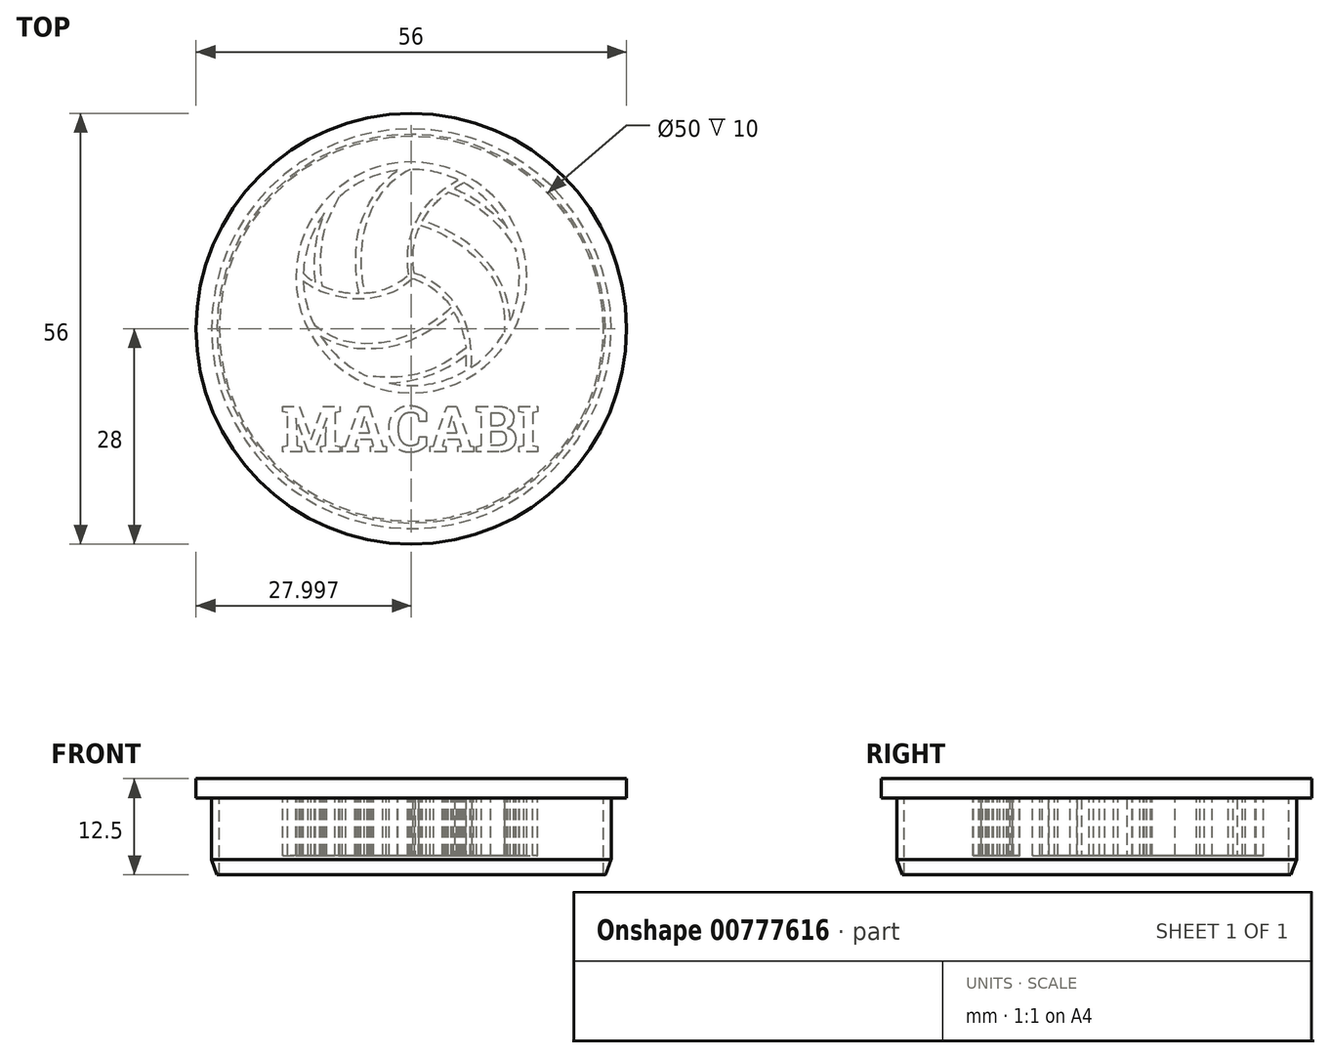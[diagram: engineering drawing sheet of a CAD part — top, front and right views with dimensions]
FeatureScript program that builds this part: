
annotation { "Feature Type Name" : "Feature", "Feature Type Description" : "" }
export const myFeature = defineFeature(function(context is Context, id is Id, definition is map)
    precondition{}
    {
        {
            var Q0;
            Q0=qCreatedBy(makeId("Top.planeOp"),FACE);
            var sketch = newSketch(context, id + "F0", { "sketchPlane" : qUnion([Q0])});
            skText(sketch, "E0", { "text": "MACABI", "fontName": "RobotoSlab-Bold.ttf"});
            skLineSegment(sketch, "E1", {"start": v(19.93, 0) * mm, "end": v(19.93, -2) * mm, "construction": true});
            skCircle(sketch, "E2", {"center": v(19.93, 8) * mm, "radius": 25 * mm});
            skCircle(sketch, "E3", {"center": v(19.93, 14.67) * mm, "radius": 15.02 * mm});
            skArc(sketch, "E4", {"start": v(5.88, 14.23) * mm, "mid": v(6.3, 11.22) * mm, "end": v(7.37, 8.37) * mm});
            skFitSpline(sketch, "E5", {"points": [v(5.88, 15.21) * mm, v(6.76, 14.44) * mm, v(7.47, 14.06) * mm], "startDerivative": vector(1.6, -1.57) * mm, "endDerivative": vector(1.55, -0.72) * mm});
            skFitSpline(sketch, "E6", {"points": [v(7.47, 14.06) * mm, v(7.32, 15.84) * mm, v(7.62, 19.54) * mm, v(8.63, 23.03) * mm], "startDerivative": vector(-0.75, 6.2) * mm, "endDerivative": vector(3.19, 9.08) * mm});
            skFitSpline(sketch, "E7", {"points": [v(10.54, 25.13) * mm, v(9.08, 22.23) * mm, v(8.5, 20.42) * mm, v(8.06, 17.25) * mm, v(8.3, 13.61) * mm], "startDerivative": vector(-6.38, -11.85) * mm, "endDerivative": vector(1.47, -13.06) * mm});
            skFitSpline(sketch, "E8", {"points": [v(8.3, 13.61) * mm, v(9.4, 13.17) * mm, v(11.17, 12.74) * mm, v(13.14, 12.61) * mm], "startDerivative": vector(3.62, -1.58) * mm, "endDerivative": vector(5.39, -0.13) * mm});
            skFitSpline(sketch, "E9", {"points": [v(13.14, 12.61) * mm, v(12.82, 14.4) * mm, v(12.75, 18.35) * mm, v(13.31, 21.53) * mm, v(15.58, 26.1) * mm, v(18.14, 28.61) * mm], "startDerivative": vector(-2.5, 10.76) * mm, "endDerivative": vector(12.97, 10.35) * mm});
            skFitSpline(sketch, "E10", {"points": [v(19.76, 28.73) * mm, v(17.86, 27.48) * mm, v(15.43, 24.73) * mm, v(13.69, 20.3) * mm, v(13.4, 15.71) * mm, v(13.82, 12.66) * mm], "startDerivative": vector(-11.79, -6.76) * mm, "endDerivative": vector(2.84, -15.6) * mm});
            skFitSpline(sketch, "E11", {"points": [v(13.82, 12.66) * mm, v(15.64, 12.9) * mm, v(17.99, 13.86) * mm, v(19.62, 15.05) * mm], "startDerivative": vector(5.63, 0.4) * mm, "endDerivative": vector(4.6, 3.81) * mm});
            skFitSpline(sketch, "E12", {"points": [v(19.62, 15.05) * mm, v(19.44, 16.92) * mm, v(19.7, 19.59) * mm, v(20.78, 22.3) * mm, v(22.31, 24.45) * mm, v(24.33, 26.3) * mm, v(25.98, 27.36) * mm], "startDerivative": vector(-1.61, 12.2) * mm, "endDerivative": vector(10.81, 6.36) * mm});
            skFitSpline(sketch, "E13", {"points": [v(25.53, 26.25) * mm, v(26.13, 26.62) * mm, v(26.73, 26.97) * mm], "startDerivative": vector(1.2, 0.74) * mm, "endDerivative": vector(1.2, 0.67) * mm});
            skFitSpline(sketch, "E14", {"points": [v(25.53, 26.25) * mm, v(27.15, 25.45) * mm, v(28.84, 24.4) * mm, v(31.71, 21.92) * mm, v(32.48, 21) * mm], "startDerivative": vector(7.16, -3.48) * mm, "endDerivative": vector(3.02, -4.25) * mm});
            skFitSpline(sketch, "E15", {"points": [v(5.88, 14.23) * mm, v(7.2, 13.37) * mm, v(9.1, 12.59) * mm, v(13.23, 11.9) * mm, v(16.42, 12.42) * mm, v(18.31, 13.2) * mm, v(20.05, 14.56) * mm], "startDerivative": vector(9.63, -6.82) * mm, "endDerivative": vector(10.86, 9.6) * mm});
            skFitSpline(sketch, "E16", {"points": [v(20.05, 14.56) * mm, v(21.78, 13.82) * mm, v(23.3, 12.8) * mm, v(24.69, 11.41) * mm, v(25.12, 10.77) * mm], "startDerivative": vector(6.5, -2.5) * mm, "endDerivative": vector(1.96, -3.34) * mm});
            skFitSpline(sketch, "E17", {"points": [v(25.12, 10.77) * mm, v(23.35, 9.3) * mm, v(20.8, 7.77) * mm, v(16.38, 6.22) * mm, v(11.34, 6.37) * mm, v(8.94, 7.39) * mm, v(7.37, 8.37) * mm], "startDerivative": vector(-12.1, -10.78) * mm, "endDerivative": vector(-10.4, 7.17) * mm});
            skFitSpline(sketch, "E18", {"points": [v(8.12, 7.06) * mm, v(10.18, 6.09) * mm, v(12.39, 5.53) * mm, v(14.36, 5.43) * mm, v(17.08, 5.67) * mm, v(19.55, 6.42) * mm, v(21.6, 7.4) * mm, v(23.7, 8.75) * mm, v(24.88, 9.66) * mm, v(25.45, 10.18) * mm], "startDerivative": vector(17.08, -9.05) * mm, "endDerivative": vector(7.68, 7.3) * mm});
            skFitSpline(sketch, "E19", {"points": [v(25.45, 10.18) * mm, v(26.1, 8.94) * mm, v(26.74, 7.07) * mm, v(27.03, 5.47) * mm], "startDerivative": vector(2.14, -3.79) * mm, "endDerivative": vector(0.67, -4.72) * mm});
            skFitSpline(sketch, "E20", {"points": [v(27.03, 5.47) * mm, v(24.36, 3.63) * mm, v(20.88, 2.15) * mm, v(17.13, 1.67) * mm, v(14.22, 1.83) * mm], "startDerivative": vector(-9.5, -7.69) * mm, "endDerivative": vector(-13.02, 1.02) * mm});
            skFitSpline(sketch, "E21", {"points": [v(17.03, 0.92) * mm, v(19.52, 1.21) * mm, v(22.5, 2.04) * mm, v(24.36, 2.85) * mm, v(25.93, 3.77) * mm, v(27.03, 4.58) * mm], "startDerivative": vector(11, 0.8) * mm, "endDerivative": vector(6.47, 5.03) * mm});
            skFitSpline(sketch, "E22", {"points": [v(27.03, 4.58) * mm, v(27.02, 3.22) * mm, v(26.97, 2.51) * mm], "startDerivative": vector(0, -2.53) * mm, "endDerivative": vector(-0.14, -1.55) * mm});
            skFitSpline(sketch, "E23", {"points": [v(27.74, 3) * mm, v(27.73, 5.1) * mm, v(27.3, 7.76) * mm, v(26.25, 10.29) * mm, v(24.11, 12.96) * mm, v(22.47, 14.19) * mm, v(21.32, 14.84) * mm, v(20.37, 15.18) * mm], "startDerivative": vector(0.43, 14.26) * mm, "endDerivative": vector(-9.6, 3) * mm});
            skFitSpline(sketch, "E24", {"points": [v(20.37, 15.18) * mm, v(20.14, 16.53) * mm, v(20.2, 18.37) * mm, v(20.54, 20.07) * mm, v(20.92, 21.07) * mm, v(21.11, 21.43) * mm], "startDerivative": vector(-1.38, 6.07) * mm, "endDerivative": vector(1.57, 2.75) * mm});
            skFitSpline(sketch, "E25", {"points": [v(21.11, 21.43) * mm, v(22.61, 20.92) * mm, v(24.6, 19.96) * mm, v(26.39, 18.86) * mm, v(28.77, 16.8) * mm, v(30.99, 13.74) * mm, v(31.91, 10.86) * mm, v(32.06, 7.58) * mm], "startDerivative": vector(13.14, -4) * mm, "endDerivative": vector(-0.03, -21.23) * mm});
            skFitSpline(sketch, "E26", {"points": [v(32.8, 9.05) * mm, v(32.35, 11.95) * mm, v(31.37, 14.38) * mm, v(29.9, 16.54) * mm, v(27.48, 18.95) * mm, v(25.8, 20.07) * mm, v(23.51, 21.23) * mm, v(21.85, 21.88) * mm, v(21.4, 22.05) * mm], "startDerivative": vector(-2.15, 20.48) * mm, "endDerivative": vector(-6.63, 2.5) * mm});
            skFitSpline(sketch, "E27", {"points": [v(21.4, 22.05) * mm, v(21.96, 22.96) * mm, v(22.87, 24.11) * mm, v(23.79, 25) * mm, v(24.75, 25.75) * mm], "startDerivative": vector(2.26, 3.82) * mm, "endDerivative": vector(4, 2.94) * mm});
            skFitSpline(sketch, "E28", {"points": [v(24.75, 25.75) * mm, v(26.43, 25.08) * mm, v(28.28, 23.97) * mm, v(30.8, 21.88) * mm, v(32.86, 19.36) * mm, v(33.53, 18.19) * mm], "startDerivative": vector(9.54, -3.48) * mm, "endDerivative": vector(3.6, -6.97) * mm});
            skArc(sketch, "E29.trimOffspring", {"start": v(8.63, 23.03) * mm, "mid": v(6.67, 19.33) * mm, "end": v(5.88, 15.21) * mm});
            skArc(sketch, "E30.trimOffspring", {"start": v(18.14, 28.61) * mm, "mid": v(14.07, 27.45) * mm, "end": v(10.54, 25.13) * mm});
            skArc(sketch, "E31.trimOffspring", {"start": v(25.98, 27.36) * mm, "mid": v(22.95, 28.4) * mm, "end": v(19.76, 28.73) * mm});
            skArc(sketch, "E32.trimOffspring", {"start": v(32.48, 21) * mm, "mid": v(30.06, 24.42) * mm, "end": v(26.73, 26.97) * mm});
            skArc(sketch, "E33.trimOffspring", {"start": v(32.8, 9.05) * mm, "mid": v(33.94, 13.56) * mm, "end": v(33.53, 18.19) * mm});
            skArc(sketch, "E34.trimOffspring", {"start": v(27.74, 3) * mm, "mid": v(30.16, 5.04) * mm, "end": v(32.06, 7.58) * mm});
            skArc(sketch, "E35.trimOffspring", {"start": v(17.03, 0.92) * mm, "mid": v(22.15, 0.8) * mm, "end": v(26.97, 2.51) * mm});
            skArc(sketch, "E36.trimOffspring", {"start": v(8.12, 7.06) * mm, "mid": v(10.78, 4) * mm, "end": v(14.22, 1.83) * mm});
            skCircle(sketch, "E37", {"center": v(19.93, 8) * mm, "radius": 26 * mm});
            skCircle(sketch, "E38", {"center": v(19.93, 8) * mm, "radius": 28 * mm});
            const initialGuessF0  = {"E0": [0.00297, -0.008, 1, 0, 0.006]};
            skSetInitialGuess(sketch, initialGuessF0);
            skSolve(sketch);
        }
        {
            var Q0;
            Q0=makeQuery(id+"F0.imprint","IMPRINT",FACE,{"disambiguationData":[TD([[makeQuery(id+"F0.imprint","IMPRINT",EDGE,{"derivedFrom":sQuery(id+"F0.wireOp",EDGE,"E0.sketch_text.stroke-111")}),1.0]])]});
            var Q1;
            Q1=makeQuery(id+"F0.imprint","IMPRINT",FACE,{"disambiguationData":[TD([[makeQuery(id+"F0.imprint","IMPRINT",EDGE,{"derivedFrom":sQuery(id+"F0.wireOp",EDGE,"E0.sketch_text.stroke-118")}),1.0]])]});
            var Q2;
            Q2=makeQuery(id+"F0.imprint","IMPRINT",FACE,{"disambiguationData":[TD([[makeQuery(id+"F0.imprint","IMPRINT",EDGE,{"derivedFrom":sQuery(id+"F0.wireOp",EDGE,"E0.sketch_text.stroke-91")}),1.0]])]});
            var Q3;
            Q3=makeQuery(id+"F0.imprint","IMPRINT",FACE,{"disambiguationData":[TD([[makeQuery(id+"F0.imprint","IMPRINT",EDGE,{"derivedFrom":sQuery(id+"F0.wireOp",EDGE,"E4")}),1.0]])]});
            var Q4;
            Q4=makeQuery(id+"F0.imprint","IMPRINT",FACE,{"disambiguationData":[TD([[makeQuery(id+"F0.imprint","IMPRINT",EDGE,{"derivedFrom":sQuery(id+"F0.wireOp",EDGE,"E10")}),1.0]])]});
            var Q5;
            Q5=makeQuery(id+"F0.imprint","IMPRINT",FACE,{"disambiguationData":[TD([[makeQuery(id+"F0.imprint","IMPRINT",EDGE,{"derivedFrom":sQuery(id+"F0.wireOp",EDGE,"E23")}),-1.0]])]});
            var Q6;
            Q6=makeQuery(id+"F0.imprint","IMPRINT",FACE,{"disambiguationData":[TD([[makeQuery(id+"F0.imprint","IMPRINT",EDGE,{"derivedFrom":sQuery(id+"F0.wireOp",EDGE,"E26")}),-1.0]])]});
            var Q7;
            Q7=makeQuery(id+"F0.imprint","IMPRINT",FACE,{"disambiguationData":[TD([[makeQuery(id+"F0.imprint","IMPRINT",EDGE,{"derivedFrom":sQuery(id+"F0.wireOp",EDGE,"E18")}),-1.0]])]});
            var Q8;
            Q8=makeQuery(id+"F0.imprint","IMPRINT",FACE,{"disambiguationData":[TD([[makeQuery(id+"F0.imprint","IMPRINT",EDGE,{"derivedFrom":sQuery(id+"F0.wireOp",EDGE,"E21")}),-1.0]])]});
            var Q9;
            Q9=makeQuery(id+"F0.imprint","IMPRINT",FACE,{"disambiguationData":[TD([[makeQuery(id+"F0.imprint","IMPRINT",EDGE,{"derivedFrom":sQuery(id+"F0.wireOp",EDGE,"E13")}),-1.0]])]});
            var Q10;
            Q10=makeQuery(id+"F0.imprint","IMPRINT",FACE,{"disambiguationData":[TD([[makeQuery(id+"F0.imprint","IMPRINT",EDGE,{"derivedFrom":sQuery(id+"F0.wireOp",EDGE,"E7")}),1.0]])]});
            var Q11;
            Q11=makeQuery(id+"F0.imprint","IMPRINT",FACE,{"disambiguationData":[TD([[makeQuery(id+"F0.imprint","IMPRINT",EDGE,{"derivedFrom":sQuery(id+"F0.wireOp",EDGE,"E5")}),1.0]])]});
            var Q12;
            Q12=makeQuery(id+"F0.imprint","IMPRINT",FACE,{"disambiguationData":[TD([[makeQuery(id+"F0.imprint","IMPRINT",EDGE,{"derivedFrom":sQuery(id+"F0.wireOp",EDGE,"E0.sketch_text.stroke-0")}),1.0]])]});
            var Q13;
            Q13=makeQuery(id+"F0.imprint","IMPRINT",FACE,{"disambiguationData":[TD([[makeQuery(id+"F0.imprint","IMPRINT",EDGE,{"derivedFrom":sQuery(id+"F0.wireOp",EDGE,"E37")}),-1.0]])]});
            var Q14;
            Q14=makeQuery(id+"F0.imprint","IMPRINT",FACE,{"disambiguationData":[TD([[makeQuery(id+"F0.imprint","IMPRINT",EDGE,{"derivedFrom":sQuery(id+"F0.wireOp",EDGE,"E0.sketch_text.stroke-47")}),1.0]])]});
            extrude(context, id + "F1", {"entities" : qUnion([Q0, Q1, Q2, Q3, Q4, Q5, Q6, Q7, Q8, Q9, Q10, Q11, Q12, Q13, Q14]), "oppositeDirection" : true, "depth" : 2.5 * mm, "offsetDistance" : 25 * mm});
        }
        {
            var Q0;
            Q0=makeQuery(id+"F0.imprint","IMPRINT",FACE,{"disambiguationData":[TD([[makeQuery(id+"F0.imprint","IMPRINT",EDGE,{"derivedFrom":sQuery(id+"F0.wireOp",EDGE,"E0.sketch_text.stroke-0")}),-1.0]])]});
            var Q1;
            Q1=makeQuery(id+"F0.imprint","IMPRINT",FACE,{"disambiguationData":[TD([[makeQuery(id+"F0.imprint","IMPRINT",EDGE,{"derivedFrom":sQuery(id+"F0.wireOp",EDGE,"E0.sketch_text.stroke-31")}),-1.0]])]});
            var Q2;
            Q2=makeQuery(id+"F0.imprint","IMPRINT",FACE,{"disambiguationData":[TD([[makeQuery(id+"F0.imprint","IMPRINT",EDGE,{"derivedFrom":sQuery(id+"F0.wireOp",EDGE,"E0.sketch_text.stroke-51")}),-1.0]])]});
            var Q3;
            Q3=makeQuery(id+"F0.imprint","IMPRINT",FACE,{"disambiguationData":[TD([[makeQuery(id+"F0.imprint","IMPRINT",EDGE,{"derivedFrom":sQuery(id+"F0.wireOp",EDGE,"E0.sketch_text.stroke-75")}),-1.0]])]});
            var Q4;
            Q4=makeQuery(id+"F0.imprint","IMPRINT",FACE,{"disambiguationData":[TD([[makeQuery(id+"F0.imprint","IMPRINT",EDGE,{"derivedFrom":sQuery(id+"F0.wireOp",EDGE,"E0.sketch_text.stroke-95")}),-1.0]])]});
            var Q5;
            Q5=makeQuery(id+"F0.imprint","IMPRINT",FACE,{"disambiguationData":[TD([[makeQuery(id+"F0.imprint","IMPRINT",EDGE,{"derivedFrom":sQuery(id+"F0.wireOp",EDGE,"E0.sketch_text.stroke-125")}),-1.0]])]});
            var Q6;
            Q6=makeQuery(id+"F0.imprint","IMPRINT",FACE,{"disambiguationData":[TD([[makeQuery(id+"F0.imprint","IMPRINT",EDGE,{"derivedFrom":sQuery(id+"F0.wireOp",EDGE,"E3")}),1.0]])]});
            extrude(context, id + "F2", {"entities" : qUnion([Q0, Q1, Q2, Q3, Q4, Q5, Q6]), "operationType" : NewBodyOperationType.ADD, "oppositeDirection" : true, "depth" : 10 * mm, "offsetDistance" : 25 * mm});
        }
        {
            var Q0;
            Q0=makeQuery(id+"F0.imprint","IMPRINT",FACE,{"disambiguationData":[TD([[makeQuery(id+"F0.imprint","IMPRINT",EDGE,{"derivedFrom":sQuery(id+"F0.wireOp",EDGE,"E2")}),-1.0]])]});
            extrude(context, id + "F3", {"entities" : qUnion([Q0]), "operationType" : NewBodyOperationType.ADD, "oppositeDirection" : true, "depth" : 12.5 * mm, "offsetDistance" : 25 * mm});
        }
        {
            var Q0;
            Q0=makeQuery(id+"F3.opExtrude","CAP_EDGE",EDGE,{"disambiguationData":[OSD([sQuery(id+"F0.wireOp",EDGE,"E37")])],"isStart":false});
            chamfer(context, id + "F4", {"entities" : qUnion([Q0]), "chamferType" : ChamferType.OFFSET_ANGLE, "width" : 2 * mm, "oppositeDirection" : false, "angle" : 20 * degree, "tangentPropagation" : true});
        }
    });
